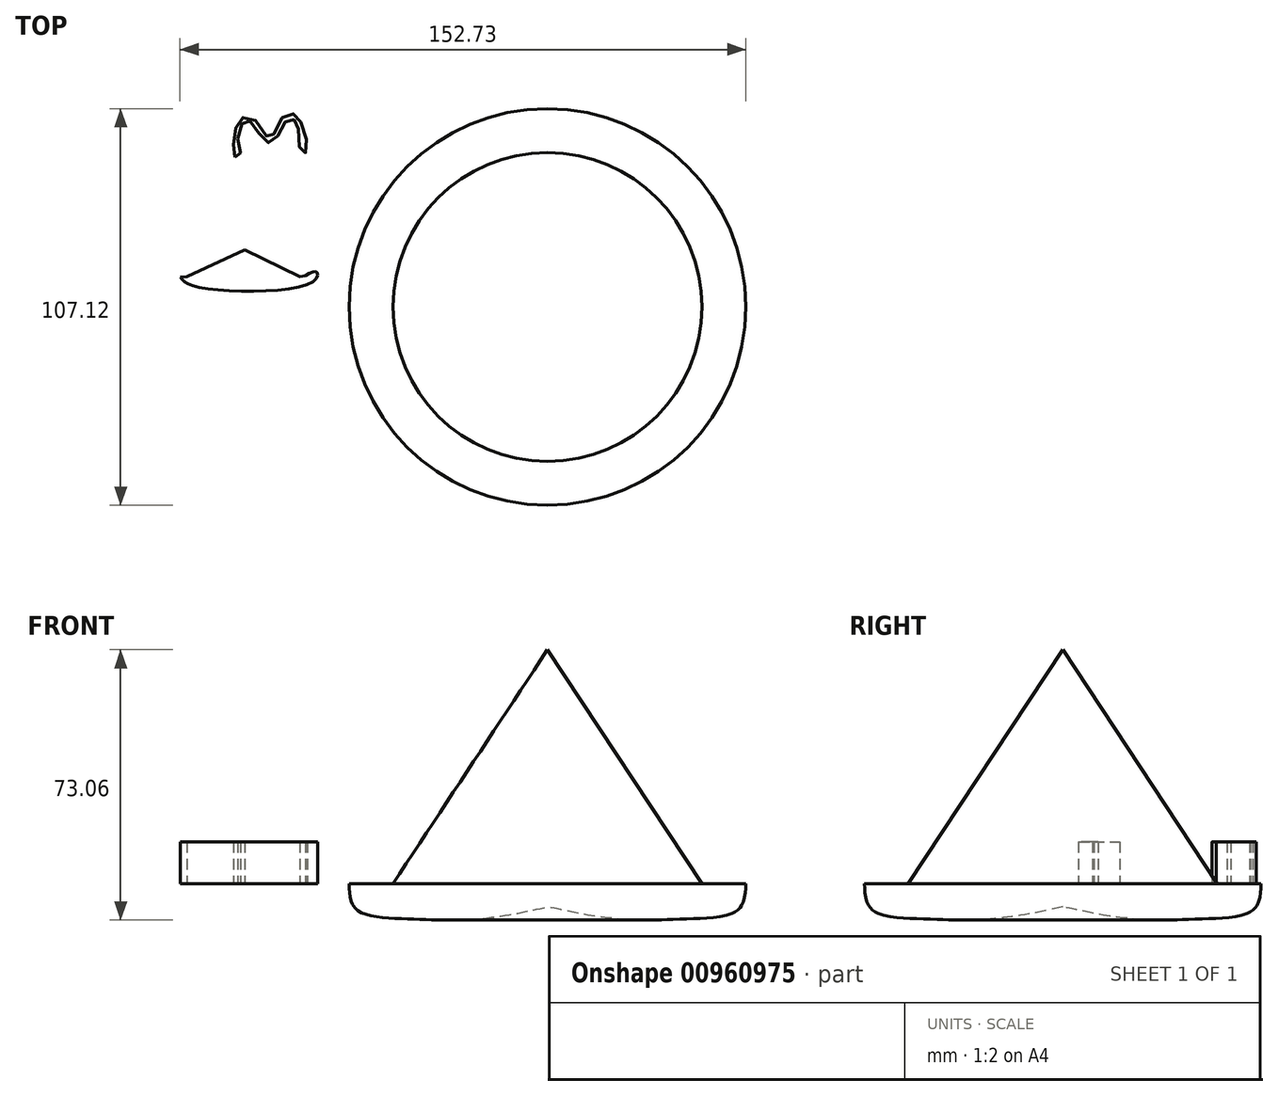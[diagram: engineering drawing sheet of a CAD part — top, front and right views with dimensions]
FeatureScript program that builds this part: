
annotation { "Feature Type Name" : "Feature", "Feature Type Description" : "" }
export const myFeature = defineFeature(function(context is Context, id is Id, definition is map)
    precondition{}
    {
        {
            var Q0;
            Q0=qCreatedBy(makeId("Front.planeOp"),FACE);
            var sketch = newSketch(context, id + "F0", { "sketchPlane" : qUnion([Q0])});
            skLineSegment(sketch, "E0", {"start": v(-41.7, 0) * mm, "end": v(0, 63.27) * mm});
            skFitSpline(sketch, "E1", {"points": [v(-53.56, 0) * mm, v(-51.47, -6.97) * mm, v(-38.05, -9.45) * mm, v(-22.8, -9.7) * mm, v(-9.38, -8.14) * mm, v(0, -6.19) * mm], "startDerivative": vector(2.35, -51.08) * mm, "endDerivative": vector(49.23, 11.12) * mm});
            skFitSpline(sketch, "E2", {"points": [v(-53.56, 0) * mm, v(-41.7, 0) * mm], "startDerivative": vector(11.86, 0) * mm, "endDerivative": vector(11.86, 0) * mm});
            skLineSegment(sketch, "E3", {"start": v(0, 63.27) * mm, "end": v(0, -6.19) * mm});
            skPoint(sketch, "E4.MirrorCS.end.orphan", {"position": v(0, 63.27) * mm});
            skPoint(sketch, "E4.MirrorCS.start.orphan", {"position": v(41.7, 0) * mm});
            skPoint(sketch, "E5.MirrorCS.start.orphan", {"position": v(53.56, 0) * mm});
            skSolve(sketch);
        }
        {
            var Q0;
            Q0 = qSketchRegion(id + "F0", true);
            var Q1;
            Q1=sQuery(id+"F0.wireOp",EDGE,"E3");
            revolve(context, id + "F1", {"surfaceOperationType" : NewSurfaceOperationType.NEW, "entities" : qUnion([Q0]), "axis" : qUnion([Q1]), "revolveType" : RevolveType.FULL});
        }
        {
            var Q0;
            Q0=qCreatedBy(makeId("Top.planeOp"),FACE);
            var sketch = newSketch(context, id + "F2", { "sketchPlane" : qUnion([Q0])});
            skFitSpline(sketch, "E6", {"points": [v(-84.31, 40.46) * mm, v(-84.57, 45.41) * mm, v(-83, 50.63) * mm, v(-79.1, 50.63) * mm, v(-74.93, 45.41) * mm, v(-71.8, 50.89) * mm, v(-68.41, 52.06) * mm, v(-66.2, 48.93) * mm, v(-65.02, 41.9) * mm, v(-66.46, 41.76) * mm, v(-67.24, 48.54) * mm, v(-68.54, 50.63) * mm, v(-70.63, 50.1) * mm, v(-73.76, 44.9) * mm, v(-76.23, 44.76) * mm, v(-79.88, 49.84) * mm, v(-81.83, 50.23) * mm, v(-83.53, 45.15) * mm, v(-83, 40.85) * mm, v(-84.31, 40.46) * mm]});
            skLineSegment(sketch, "E7", {"start": v(-81.7, 15.44) * mm, "end": v(-97.34, 8.14) * mm});
            skLineSegment(sketch, "E8", {"start": v(-97.34, 8.14) * mm, "end": v(-66.88, 8.14) * mm});
            skLineSegment(sketch, "E9", {"start": v(-66.88, 8.14) * mm, "end": v(-81.7, 15.44) * mm});
            skFitSpline(sketch, "E10", {"points": [v(-99.17, 8.01) * mm, v(-94.6, 5.4) * mm, v(-63.2, 6.84) * mm, v(-62.29, 9.45) * mm, v(-65.94, 8.14) * mm], "startDerivative": vector(12.44, -14.41) * mm, "endDerivative": vector(-26.41, -15.17) * mm});
            skFitSpline(sketch, "E11", {"points": [v(-65.36, 8.47) * mm, v(-66.88, 8.14) * mm], "startDerivative": vector(-1.52, -0.33) * mm, "endDerivative": vector(-1.52, -0.33) * mm});
            skFitSpline(sketch, "E12", {"points": [v(-99.17, 8.01) * mm, v(-97.34, 8.14) * mm], "startDerivative": vector(1.82, 0.13) * mm, "endDerivative": vector(1.82, 0.13) * mm});
            skSolve(sketch);
        }
        {
            var Q0;
            Q0 = qSketchRegion(id + "F2", true);
            extrude(context, id + "F3", {"entities" : qUnion([Q0]), "depth" : 11.4 * mm, "offsetDistance" : 25.4 * mm});
        }
    });
